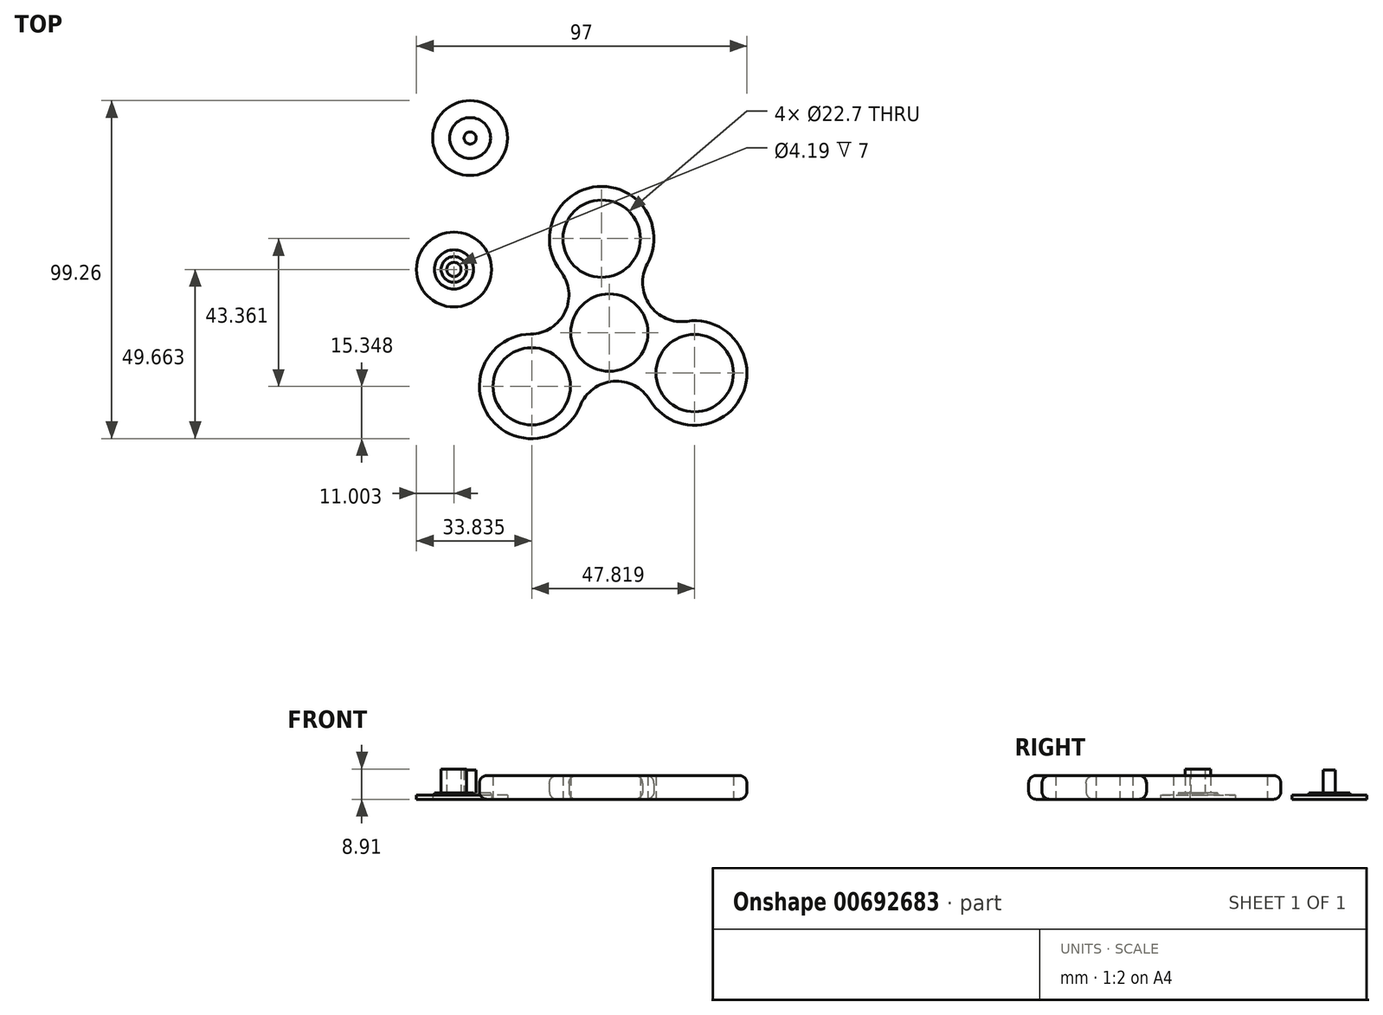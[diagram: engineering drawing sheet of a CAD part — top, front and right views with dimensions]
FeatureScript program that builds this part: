
annotation { "Feature Type Name" : "Feature", "Feature Type Description" : "" }
export const myFeature = defineFeature(function(context is Context, id is Id, definition is map)
    precondition{}
    {
        {
            var Q0;
            Q0=qCreatedBy(makeId("Top.planeOp"),FACE);
            var sketch = newSketch(context, id + "F0", { "sketchPlane" : qUnion([Q0])});
            skCircle(sketch, "E0", {"center": v(0, 0) * mm, "radius": 11.35 * mm});
            skCircle(sketch, "E1", {"center": v(-22.79, -15.75) * mm, "radius": 11.35 * mm});
            skCircle(sketch, "E2", {"center": v(25.03, -11.86) * mm, "radius": 11.35 * mm});
            skCircle(sketch, "E3", {"center": v(-2.25, 27.6) * mm, "radius": 11.35 * mm});
            skCircle(sketch, "E4.0", {"center": v(-22.79, -15.75) * mm, "radius": 15.35 * mm});
            skCircle(sketch, "E5.0", {"center": v(-2.25, 27.6) * mm, "radius": 15.35 * mm});
            skCircle(sketch, "E6.0", {"center": v(25.03, -11.86) * mm, "radius": 15.35 * mm});
            skLineSegment(sketch, "E7", {"start": v(-16.21, -1.88) * mm, "end": v(-8.82, 13.74) * mm, "construction": true});
            skLineSegment(sketch, "E8", {"start": v(16.3, 0.77) * mm, "end": v(6.48, 14.98) * mm, "construction": true});
            skLineSegment(sketch, "E9", {"start": v(-7.49, -14.5) * mm, "end": v(9.73, -13.1) * mm, "construction": true});
            skArc(sketch, "E10", {"start": v(11.9, -19.8) * mm, "mid": v(1.17, -14.3) * mm, "end": v(-8.54, -21.46) * mm});
            skArc(sketch, "E11", {"start": v(-23.1, -0.4) * mm, "mid": v(-12.97, 6.14) * mm, "end": v(-14.32, 18.12) * mm});
            skArc(sketch, "E12", {"start": v(11.2, 20.2) * mm, "mid": v(11.8, 8.16) * mm, "end": v(22.85, 3.34) * mm});
            skSolve(sketch);
        }
        {
            var Q0;
            Q0=makeQuery(id+"F0.imprint","IMPRINT",FACE,{"disambiguationData":[TD([[makeQuery(id+"F0.imprint","IMPRINT",EDGE,{"derivedFrom":sQuery(id+"F0.wireOp",EDGE,"E1")}),-1.0]])]});
            var Q1;
            Q1=makeQuery(id+"F0.imprint","IMPRINT",FACE,{"disambiguationData":[TD([[makeQuery(id+"F0.imprint","IMPRINT",EDGE,{"derivedFrom":sQuery(id+"F0.wireOp",EDGE,"E0")}),-1.0]])]});
            var Q2;
            Q2=makeQuery(id+"F0.imprint","IMPRINT",FACE,{"disambiguationData":[TD([[makeQuery(id+"F0.imprint","IMPRINT",EDGE,{"derivedFrom":sQuery(id+"F0.wireOp",EDGE,"E3")}),-1.0]])]});
            var Q3;
            Q3=makeQuery(id+"F0.imprint","IMPRINT",FACE,{"disambiguationData":[TD([[makeQuery(id+"F0.imprint","IMPRINT",EDGE,{"derivedFrom":sQuery(id+"F0.wireOp",EDGE,"E2")}),-1.0]])]});
            extrude(context, id + "F1", {"entities" : qUnion([Q0, Q1, Q2, Q3]), "depth" : 7 * mm, "offsetDistance" : 25.4 * mm});
        }
        {
            var Q0;
            Q0=makeQuery(id+"F1.opExtrude","CAP_EDGE",EDGE,{"disambiguationData":[OSD([sQuery(id+"F0.wireOp",EDGE,"E4.0")])],"isStart":false});
            fillet(context, id + "F2", {"entities" : qUnion([Q0]), "radius" : 2.3 * mm, "tangentPropagation" : true, "allowEdgeOverflow" : false});
        }
        {
            var Q0;
            Q0=makeQuery(id+"F1.opExtrude","CAP_EDGE",EDGE,{"disambiguationData":[OSD([sQuery(id+"F0.wireOp",EDGE,"E5.0")])],"isStart":true});
            fillet(context, id + "F3", {"entities" : qUnion([Q0]), "radius" : 2.3 * mm, "tangentPropagation" : true, "allowEdgeOverflow" : false});
        }
        {
            var Q0;
            Q0=qCreatedBy(makeId("Top.planeOp"),FACE);
            var sketch = newSketch(context, id + "F4", { "sketchPlane" : qUnion([Q0])});
            skCircle(sketch, "E13", {"center": v(-45.62, 18.56) * mm, "radius": 11 * mm});
            skCircle(sketch, "E14.0", {"center": v(-45.62, 18.56) * mm, "radius": 3.75 * mm});
            skCircle(sketch, "E15.0", {"center": v(-45.62, 18.56) * mm, "radius": 5.75 * mm});
            skCircle(sketch, "E16", {"center": v(-45.62, 18.56) * mm, "radius": 2.1 * mm});
            skSolve(sketch);
        }
        {
            var Q0;
            Q0=makeQuery(id+"F4.imprint","IMPRINT",FACE,{"disambiguationData":[TD([[makeQuery(id+"F4.imprint","IMPRINT",EDGE,{"derivedFrom":sQuery(id+"F4.wireOp",EDGE,"E13")}),1.0]])]});
            extrude(context, id + "F5", {"entities" : qUnion([Q0]), "depth" : 1.27 * mm, "offsetDistance" : 25.4 * mm});
        }
        {
            var Q0;
            Q0=makeQuery(id+"F4.imprint","IMPRINT",FACE,{"disambiguationData":[TD([[makeQuery(id+"F4.imprint","IMPRINT",EDGE,{"derivedFrom":sQuery(id+"F4.wireOp",EDGE,"E14.0")}),-1.0]])]});
            var Q1;
            Q1=makeQuery(id+"F4.imprint","IMPRINT",FACE,{"disambiguationData":[TD([[makeQuery(id+"F4.imprint","IMPRINT",EDGE,{"derivedFrom":sQuery(id+"F4.wireOp",EDGE,"E16")}),1.0]])]});
            extrude(context, id + "F6", {"entities" : qUnion([Q0, Q1]), "operationType" : NewBodyOperationType.ADD, "depth" : 1.9 * mm, "offsetDistance" : 25.4 * mm});
        }
        {
            var Q0;
            Q0=makeQuery(id+"F4.imprint","IMPRINT",FACE,{"disambiguationData":[TD([[makeQuery(id+"F4.imprint","IMPRINT",EDGE,{"derivedFrom":sQuery(id+"F4.wireOp",EDGE,"E14.0")}),1.0]])]});
            extrude(context, id + "F7", {"entities" : qUnion([Q0]), "operationType" : NewBodyOperationType.ADD, "depth" : 8.9 * mm, "offsetDistance" : 25.4 * mm});
        }
        {
            var Q0;
            Q0=qCreatedBy(makeId("Top.planeOp"),FACE);
            var sketch = newSketch(context, id + "F8", { "sketchPlane" : qUnion([Q0])});
            skCircle(sketch, "E17", {"center": v(-40.87, 57.16) * mm, "radius": 11 * mm});
            skCircle(sketch, "E18", {"center": v(-40.87, 57.16) * mm, "radius": 6 * mm});
            skCircle(sketch, "E19", {"center": v(-40.87, 57.16) * mm, "radius": 1.78 * mm});
            skSolve(sketch);
        }
        {
            var Q0;
            Q0=makeQuery(id+"F8.imprint","IMPRINT",FACE,{"disambiguationData":[TD([[makeQuery(id+"F8.imprint","IMPRINT",EDGE,{"derivedFrom":sQuery(id+"F8.wireOp",EDGE,"E17")}),1.0]])]});
            extrude(context, id + "F9", {"entities" : qUnion([Q0]), "depth" : 1.27 * mm, "offsetDistance" : 25.4 * mm});
        }
        {
            var Q0;
            Q0=makeQuery(id+"F8.imprint","IMPRINT",FACE,{"disambiguationData":[TD([[makeQuery(id+"F8.imprint","IMPRINT",EDGE,{"derivedFrom":sQuery(id+"F8.wireOp",EDGE,"E18")}),1.0]])]});
            extrude(context, id + "F10", {"entities" : qUnion([Q0]), "operationType" : NewBodyOperationType.ADD, "depth" : 1.9 * mm, "offsetDistance" : 25.4 * mm});
        }
        {
            var Q0;
            Q0=makeQuery(id+"F8.imprint","IMPRINT",FACE,{"disambiguationData":[TD([[makeQuery(id+"F8.imprint","IMPRINT",EDGE,{"derivedFrom":sQuery(id+"F8.wireOp",EDGE,"E19")}),1.0]])]});
            extrude(context, id + "F11", {"entities" : qUnion([Q0]), "operationType" : NewBodyOperationType.ADD, "depth" : 8.65 * mm, "offsetDistance" : 25.4 * mm});
        }
    });
